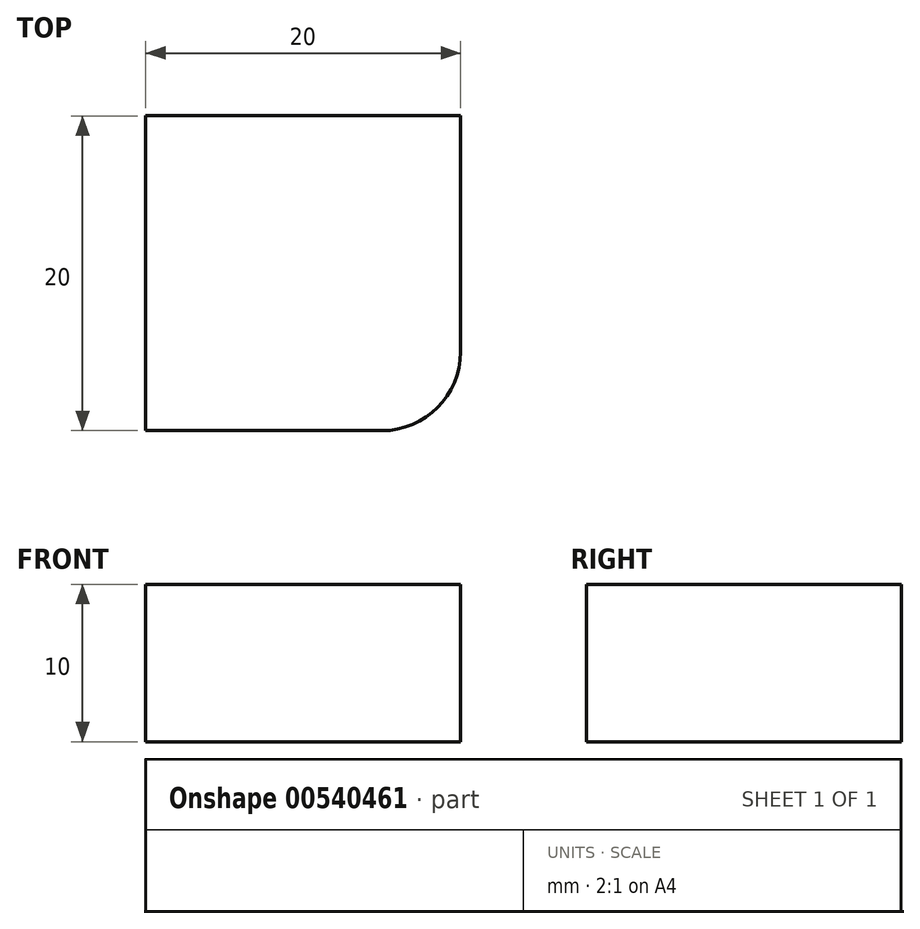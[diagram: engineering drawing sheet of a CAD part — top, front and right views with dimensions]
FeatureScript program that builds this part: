
annotation { "Feature Type Name" : "Feature", "Feature Type Description" : "" }
export const myFeature = defineFeature(function(context is Context, id is Id, definition is map)
    precondition{}
    {
        {
            var Q0;
            Q0=qCreatedBy(makeId("Top.planeOp"),FACE);
            var sketch = newSketch(context, id + "F0", { "sketchPlane" : qUnion([Q0])});
            skLineSegment(sketch, "E0.bottom", {"start": v(-54.91, -4.75) * mm, "end": v(-34.91, -4.75) * mm});
            skLineSegment(sketch, "E0.top", {"start": v(-54.91, -24.75) * mm, "end": v(-39.91, -24.75) * mm});
            skLineSegment(sketch, "E0.left", {"start": v(-54.91, -4.75) * mm, "end": v(-54.91, -24.75) * mm});
            skLineSegment(sketch, "E0.right", {"start": v(-34.91, -4.75) * mm, "end": v(-34.91, -19.75) * mm});
            skPoint(sketch, "E0.middle", {"position": v(-44.91, -14.75) * mm});
            skPoint(sketch, "E1.visualSharp", {"position": v(-34.91, -24.75) * mm});
            skArc(sketch, "E1.filletArc", {"start": v(-39.91, -24.75) * mm, "mid": v(-36.38, -23.28) * mm, "end": v(-34.91, -19.75) * mm});
            skCircle(sketch, "E2", {"center": v(-44.91, -14.75) * mm, "radius": 6.46 * mm});
            skSolve(sketch);
        }
        {
            var Q0;
            Q0=makeQuery(id+"F0.imprint","IMPRINT",FACE,{"disambiguationData":[TD([[makeQuery(id+"F0.imprint","IMPRINT",EDGE,{"derivedFrom":sQuery(id+"F0.wireOp",EDGE,"E2")}),1.0]])]});
            var Q1;
            Q1=makeQuery(id+"F0.imprint","IMPRINT",FACE,{"disambiguationData":[TD([[makeQuery(id+"F0.imprint","IMPRINT",EDGE,{"derivedFrom":sQuery(id+"F0.wireOp",EDGE,"E0.bottom")}),-1.0]])]});
            extrude(context, id + "F1", {"entities" : qUnion([Q0, Q1]), "depth" : 10 * mm, "offsetDistance" : 25 * mm});
        }
        {
            var Q0;
            Q0=makeQuery(id+"F0.imprint","IMPRINT",FACE,{"disambiguationData":[TD([[makeQuery(id+"F0.imprint","IMPRINT",EDGE,{"derivedFrom":sQuery(id+"F0.wireOp",EDGE,"E0.bottom")}),-1.0]])]});
            extrude(context, id + "F2", {"entities" : qUnion([Q0]), "operationType" : NewBodyOperationType.ADD, "depth" : 10 * mm, "offsetDistance" : 25 * mm});
        }
    });
